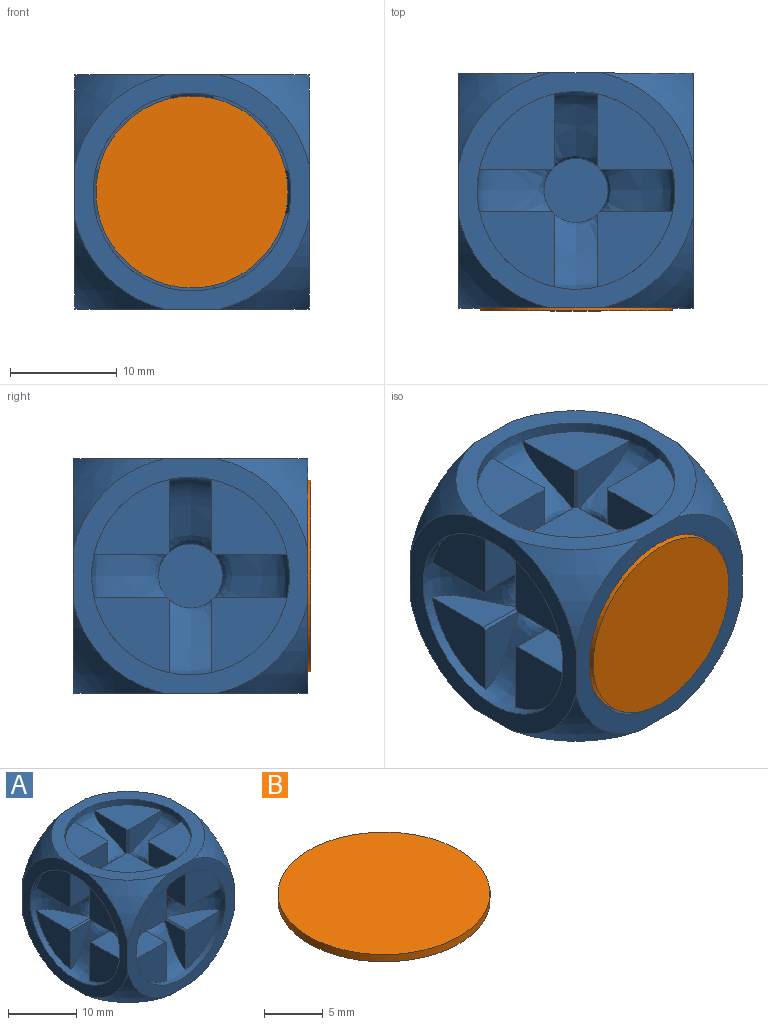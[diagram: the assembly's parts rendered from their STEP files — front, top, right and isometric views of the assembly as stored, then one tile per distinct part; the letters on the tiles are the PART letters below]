
ASSEMBLY  parts=2 mates=1
PART A: 122 faces, bbox 32.2x32.2x23.9 mm
  f0: bspline ~19.33x19.33mm, area 231.4mm2, adj f63,f105,f106,f107,f108,f110,f111,f112
  f1: bspline ~19.33x19.33mm, area 231.4mm2, adj f2,f88,f89,f90,f91,f93,f94,f96
  f2: plane 22x22mm, normal (0,0,-1), area 125.5mm2, adj f1,f58,f60,f61,f62,f64,f65,f66
  f3: plane 8.69x6.87mm, normal (0,1,0), area 19.3mm2, adj f4,f6,f20
  f4: extruded ~5x0.24mm, area 1.7mm2, adj f3,f5,f6,f19
  f5: plane 8.69x6.87mm, normal (0,0,1), area 19.3mm2, adj f4,f6,f20
  f6: plane 7.06x7.06mm, normal (-1,0,0), area 34.7mm2, adj f3,f4,f5,f20
  f7: plane 8.69x6.87mm, normal (0,-1,0), area 19.3mm2, adj f9,f10,f20
  f8: plane 8.69x6.87mm, normal (0,0,1), area 19.3mm2, adj f9,f10,f20
  f9: extruded ~5x0.24mm, area 1.7mm2, adj f7,f8,f10,f19
  f10: plane 7.06x7.06mm, normal (-1,0,0), area 34.7mm2, adj f7,f8,f9,f20
  f11: plane 8.69x6.87mm, normal (0,0,-1), area 19.3mm2, adj f12,f14,f20
  f12: extruded ~5x0.24mm, area 1.7mm2, adj f11,f13,f14,f19
  f13: plane 8.69x6.87mm, normal (0,-1,0), area 19.3mm2, adj f12,f14,f20
  f14: plane 7.06x7.06mm, normal (-1,0,0), area 34.7mm2, adj f11,f12,f13,f20
  f15: extruded ~5x0.24mm, area 1.7mm2, adj f16,f17,f18,f19
  f16: plane 8.69x6.87mm, normal (0,1,0), area 19.3mm2, adj f15,f18,f20
  f17: plane 8.69x6.87mm, normal (0,0,-1), area 19.3mm2, adj f15,f18,f20
  f18: plane 7.06x7.06mm, normal (-1,0,0), area 34.7mm2, adj f15,f16,f17,f20
  f19: plane 6x6mm, normal (-1,0,0), area 28.3mm2, adj f4,f9,f12,f15,f20
  f20: bspline ~19.33x19.33mm, area 231.4mm2, adj f3,f5,f6,f7,f8,f10,f11,f13
  f21: plane 8.69x6.87mm, normal (-1,0,0), area 19.3mm2, adj f22,f24,f38
  f22: extruded ~5x0.24mm, area 1.7mm2, adj f21,f23,f24,f37
  f23: plane 8.69x6.87mm, normal (0,0,1), area 19.3mm2, adj f22,f24,f38
  f24: plane 7.06x7.06mm, normal (0,-1,0), area 34.7mm2, adj f21,f22,f23,f38
  f25: plane 8.69x6.87mm, normal (1,0,0), area 19.3mm2, adj f27,f28,f38
  f26: plane 8.69x6.87mm, normal (0,0,1), area 19.3mm2, adj f27,f28,f38
  f27: extruded ~5x0.24mm, area 1.7mm2, adj f25,f26,f28,f37
  f28: plane 7.06x7.06mm, normal (0,-1,0), area 34.7mm2, adj f25,f26,f27,f38
  f29: plane 8.69x6.87mm, normal (0,0,-1), area 19.3mm2, adj f30,f32,f38
  f30: extruded ~5x0.24mm, area 1.7mm2, adj f29,f31,f32,f37
  f31: plane 8.69x6.87mm, normal (1,0,0), area 19.3mm2, adj f30,f32,f38
  f32: plane 7.06x7.06mm, normal (0,-1,0), area 34.7mm2, adj f29,f30,f31,f38
  f33: extruded ~5x0.24mm, area 1.7mm2, adj f34,f35,f36,f37
  f34: plane 8.69x6.87mm, normal (-1,0,0), area 19.3mm2, adj f33,f36,f38
  f35: plane 8.69x6.87mm, normal (0,0,-1), area 19.3mm2, adj f33,f36,f38
  f36: plane 7.06x7.06mm, normal (0,-1,0), area 34.7mm2, adj f33,f34,f35,f38
  f37: plane 6x6mm, normal (0,-1,0), area 28.3mm2, adj f22,f27,f30,f33,f38
  f38: bspline ~19.33x19.33mm, area 231.4mm2, adj f21,f23,f24,f25,f26,f28,f29,f31
  f39: plane 8.69x6.87mm, normal (0,-1,0), area 19.3mm2, adj f40,f42,f56
  f40: extruded ~5x0.24mm, area 1.7mm2, adj f39,f41,f42,f55
  f41: plane 8.69x6.87mm, normal (0,0,1), area 19.3mm2, adj f40,f42,f56
  f42: plane 7.06x7.06mm, normal (1,0,0), area 34.7mm2, adj f39,f40,f41,f56
  f43: plane 8.69x6.87mm, normal (0,1,0), area 19.3mm2, adj f45,f46,f56
  f44: plane 8.69x6.87mm, normal (0,0,1), area 19.3mm2, adj f45,f46,f56
  f45: extruded ~5x0.24mm, area 1.7mm2, adj f43,f44,f46,f55
  f46: plane 7.06x7.06mm, normal (1,0,0), area 34.7mm2, adj f43,f44,f45,f56
  f47: plane 8.69x6.87mm, normal (0,0,-1), area 19.3mm2, adj f48,f50,f56
  f48: extruded ~5x0.24mm, area 1.7mm2, adj f47,f49,f50,f55
  f49: plane 8.69x6.87mm, normal (0,1,0), area 19.3mm2, adj f48,f50,f56
  f50: plane 7.06x7.06mm, normal (1,0,0), area 34.7mm2, adj f47,f48,f49,f56
  f51: extruded ~5x0.24mm, area 1.7mm2, adj f52,f53,f54,f55
  f52: plane 8.69x6.87mm, normal (0,-1,0), area 19.3mm2, adj f51,f54,f56
  f53: plane 8.69x6.87mm, normal (0,0,-1), area 19.3mm2, adj f51,f54,f56
  f54: plane 7.06x7.06mm, normal (1,0,0), area 34.7mm2, adj f51,f52,f53,f56
  f55: plane 6x6mm, normal (1,0,0), area 28.3mm2, adj f40,f45,f48,f51,f56
  f56: bspline ~19.33x19.33mm, area 231.4mm2, adj f39,f41,f42,f43,f44,f46,f47,f49
  f57: bspline ~19.33x19.33mm, area 231.4mm2, adj f58,f71,f72,f73,f75,f76,f77,f78
  f58: plane 22x22mm, normal (0,1,0), area 125.5mm2, adj f2,f57,f60,f61,f63,f64,f65,f68
  f59: sphere r=15.75mm, area 39mm2, adj f60,f62,f63
  f60: plane 22x22mm, normal (1,0,0), area 125.5mm2, adj f2,f56,f58,f59,f62,f63,f64,f67
  f61: plane 22x22mm, normal (-1,0,0), area 125.5mm2, adj f2,f20,f58,f62,f63,f65,f66,f69
  f62: plane 22x22mm, normal (0,-1,0), area 125.5mm2, adj f2,f38,f59,f60,f61,f63,f66,f67
  f63: plane 22x22mm, normal (0,0,1), area 125.5mm2, adj f0,f58,f59,f60,f61,f62,f68,f69
  f64: sphere r=15.75mm, area 39mm2, adj f2,f58,f60
  f65: sphere r=15.75mm, area 39mm2, adj f2,f58,f61
  f66: sphere r=15.75mm, area 39mm2, adj f2,f61,f62
  f67: sphere r=15.75mm, area 39mm2, adj f2,f60,f62
  f68: sphere r=15.75mm, area 39mm2, adj f58,f60,f63
  f69: sphere r=15.75mm, area 39mm2, adj f58,f61,f63
  f70: sphere r=15.75mm, area 39mm2, adj f61,f62,f63
  f71: plane 6x6mm, normal (0,1,0), area 28.3mm2, adj f57,f74,f79,f82,f86
  f72: plane 8.69x6.87mm, normal (0,0,-1), area 19.3mm2, adj f57,f74,f75
  f73: plane 8.69x6.87mm, normal (1,0,0), area 19.3mm2, adj f57,f74,f75
  f74: extruded ~5x0.24mm, area 1.7mm2, adj f71,f72,f73,f75
  f75: plane 7.06x7.06mm, normal (0,1,0), area 34.7mm2, adj f57,f72,f73,f74
  f76: plane 8.69x6.87mm, normal (0,0,1), area 19.3mm2, adj f57,f78,f79
  f77: plane 8.69x6.87mm, normal (1,0,0), area 19.3mm2, adj f57,f78,f79
  f78: plane 7.06x7.06mm, normal (0,1,0), area 34.7mm2, adj f57,f76,f77,f79
  f79: extruded ~5x0.24mm, area 1.7mm2, adj f71,f76,f77,f78
  f80: plane 8.69x6.87mm, normal (0,0,1), area 19.3mm2, adj f57,f82,f83
  f81: plane 8.69x6.87mm, normal (-1,0,0), area 19.3mm2, adj f57,f82,f83
  f82: extruded ~5x0.24mm, area 1.7mm2, adj f71,f80,f81,f83
  f83: plane 7.06x7.06mm, normal (0,1,0), area 34.7mm2, adj f57,f80,f81,f82
  f84: plane 8.69x6.87mm, normal (0,0,-1), area 19.3mm2, adj f57,f86,f87
  f85: plane 8.69x6.87mm, normal (-1,0,0), area 19.3mm2, adj f57,f86,f87
  f86: extruded ~5x0.24mm, area 1.7mm2, adj f71,f84,f85,f87
  f87: plane 7.06x7.06mm, normal (0,1,0), area 34.7mm2, adj f57,f84,f85,f86
  f88: plane 6x6mm, normal (0,0,-1), area 28.3mm2, adj f1,f92,f95,f100,f104
  f89: plane 8.69x6.87mm, normal (0,1,0), area 19.3mm2, adj f1,f91,f92
  f90: plane 8.69x6.87mm, normal (-1,0,0), area 19.3mm2, adj f1,f91,f92
  f91: plane 7.06x7.06mm, normal (0,0,-1), area 34.7mm2, adj f1,f89,f90,f92
  f92: extruded ~5x0.24mm, area 1.7mm2, adj f88,f89,f90,f91
  f93: plane 8.69x6.87mm, normal (1,0,0), area 19.3mm2, adj f1,f95,f96
  f94: plane 8.69x6.87mm, normal (0,1,0), area 19.3mm2, adj f1,f95,f96
  f95: extruded ~5x0.24mm, area 1.7mm2, adj f88,f93,f94,f96
  f96: plane 7.06x7.06mm, normal (0,0,-1), area 34.7mm2, adj f1,f93,f94,f95
  f97: plane 8.69x6.87mm, normal (-1,0,0), area 19.3mm2, adj f1,f99,f100
  f98: plane 8.69x6.87mm, normal (0,-1,0), area 19.3mm2, adj f1,f99,f100
  f99: plane 7.06x7.06mm, normal (0,0,-1), area 34.7mm2, adj f1,f97,f98,f100
  f100: extruded ~5x0.24mm, area 1.7mm2, adj f88,f97,f98,f99
  f101: plane 8.69x6.87mm, normal (1,0,0), area 19.3mm2, adj f1,f103,f104
  f102: plane 8.69x6.87mm, normal (0,-1,0), area 19.3mm2, adj f1,f103,f104
  f103: plane 7.06x7.06mm, normal (0,0,-1), area 34.7mm2, adj f1,f101,f102,f104
  f104: extruded ~5x0.24mm, area 1.7mm2, adj f88,f101,f102,f103
  f105: plane 6x6mm, normal (0,0,1), area 28.3mm2, adj f0,f109,f113,f116,f121
  f106: plane 8.69x6.87mm, normal (-1,0,0), area 19.3mm2, adj f0,f108,f109
  f107: plane 8.69x6.87mm, normal (0,1,0), area 19.3mm2, adj f0,f108,f109
  f108: plane 7.06x7.06mm, normal (0,0,1), area 34.7mm2, adj f0,f106,f107,f109
  f109: extruded ~5x0.24mm, area 1.7mm2, adj f105,f106,f107,f108
  f110: plane 8.69x6.87mm, normal (0,1,0), area 19.3mm2, adj f0,f112,f113
  f111: plane 8.69x6.87mm, normal (1,0,0), area 19.3mm2, adj f0,f112,f113
  f112: plane 7.06x7.06mm, normal (0,0,1), area 34.7mm2, adj f0,f110,f111,f113
  f113: extruded ~5x0.24mm, area 1.7mm2, adj f105,f110,f111,f112
  f114: plane 8.69x6.87mm, normal (-1,0,0), area 19.3mm2, adj f0,f116,f117
  f115: plane 8.69x6.87mm, normal (0,-1,0), area 19.3mm2, adj f0,f116,f117
  f116: extruded ~5x0.24mm, area 1.7mm2, adj f105,f114,f115,f117
  f117: plane 7.06x7.06mm, normal (0,0,1), area 34.7mm2, adj f0,f114,f115,f116
  f118: plane 8.69x6.87mm, normal (0,-1,0), area 19.3mm2, adj f0,f120,f121
  f119: plane 8.69x6.87mm, normal (1,0,0), area 19.3mm2, adj f0,f120,f121
  f120: plane 7.06x7.06mm, normal (0,0,1), area 34.7mm2, adj f0,f118,f119,f121
  f121: extruded ~5x0.24mm, area 1.7mm2, adj f105,f118,f119,f120
PART B: 6 faces, bbox 18x18x4.8 mm
  f0: cylinder r=9mm len=18mm, axis (0,0,-1), area 42.4mm2, adj f1,f2
  f1: plane 18x18mm, normal (0,0,1), area 254.5mm2, adj f0
  f2: plane 18x18mm, normal (0,0,-1), area 227.1mm2, adj f0,f3
  f3: cylinder r=2.95mm len=5.9mm, axis (0,0,1), area 70.4mm2, adj f2,f5
  f4: plane 5.5x5.5mm, normal (0,0,-1), area 23.8mm2, adj f5
  f5: cone r=2.95mm half-angle=45deg, axis (0,0,1), area 5.1mm2, adj f3,f4
PLACE A t=(-3.28,0.8,4.05)mm
PLACE B rot(axis=(1,0,0),90deg) t=(-3.28,-9.72,4.05)mm
MATE slider B.f3 <-> A.f37  axis (0,-1,0) through (-3.28,-5.92,4.05)mm
